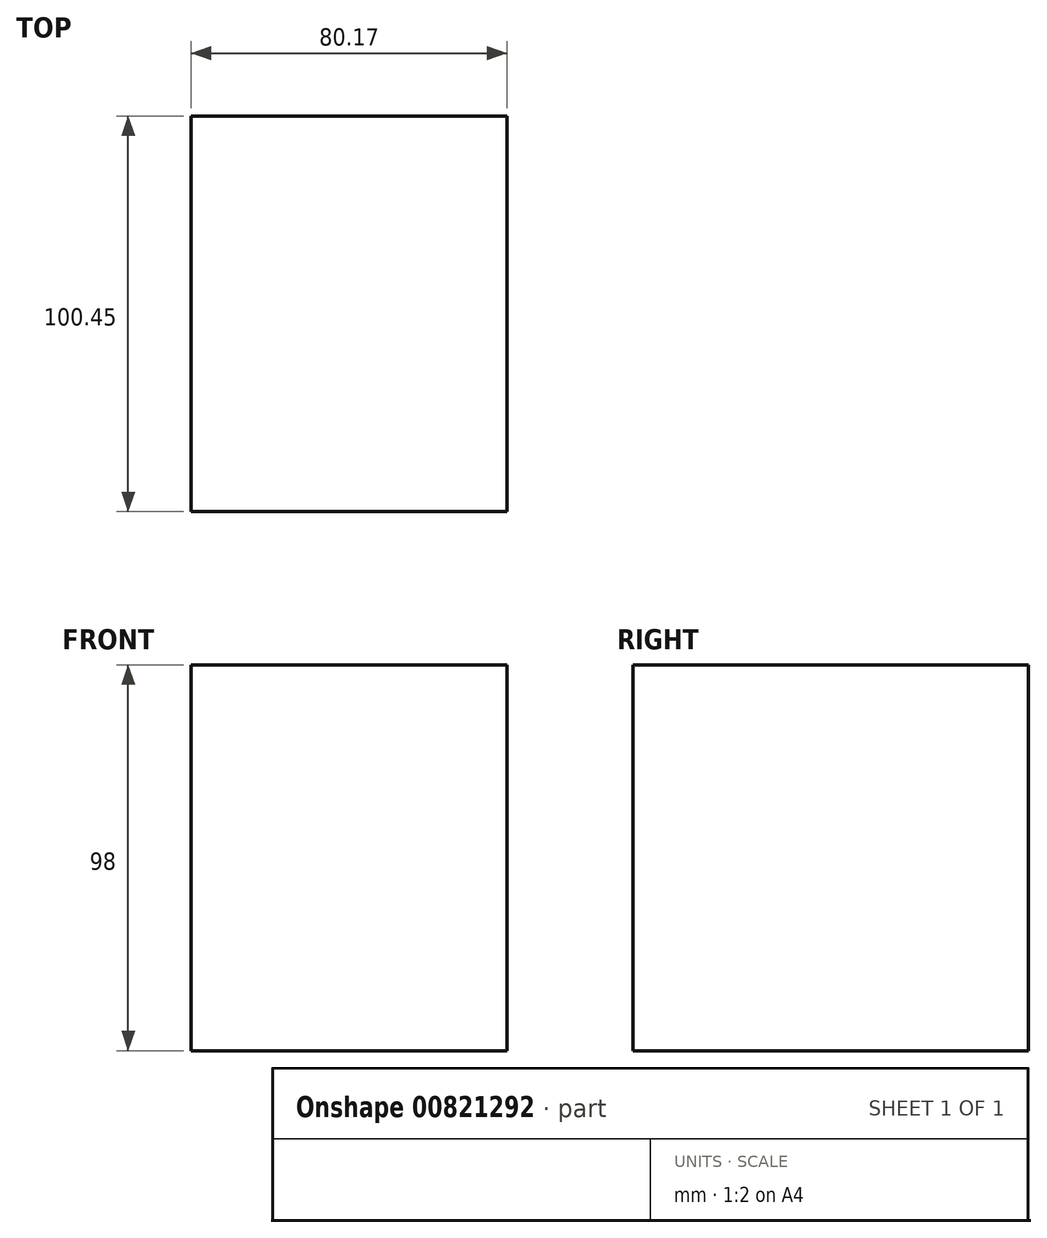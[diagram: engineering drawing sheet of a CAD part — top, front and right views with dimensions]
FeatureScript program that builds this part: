
annotation { "Feature Type Name" : "Feature", "Feature Type Description" : "" }
export const myFeature = defineFeature(function(context is Context, id is Id, definition is map)
    precondition{}
    {
        {
            var Q0;
            Q0=qCreatedBy(makeId("Top.planeOp"),FACE);
            var sketch = newSketch(context, id + "F0", { "sketchPlane" : qUnion([Q0])});
            skLineSegment(sketch, "E0.bottom", {"start": v(-100.89, 80.83) * mm, "end": v(-20.72, 80.83) * mm});
            skLineSegment(sketch, "E0.top", {"start": v(-100.89, -19.62) * mm, "end": v(-20.72, -19.62) * mm});
            skLineSegment(sketch, "E0.left", {"start": v(-100.89, 80.83) * mm, "end": v(-100.89, -19.62) * mm});
            skLineSegment(sketch, "E0.right", {"start": v(-20.72, 80.83) * mm, "end": v(-20.72, -19.62) * mm});
            skSolve(sketch);
        }
        {
            var Q0;
            Q0=makeQuery(id+"F0.imprint","IMPRINT",FACE,{"disambiguationData":[TD([[makeQuery(id+"F0.imprint","IMPRINT",EDGE,{"derivedFrom":sQuery(id+"F0.wireOp",EDGE,"E0.bottom")}),-1.0]])]});
            extrude(context, id + "F1", {"entities" : qUnion([Q0]), "depth" : 98 * mm, "offsetDistance" : 25.4 * mm});
        }
    });
